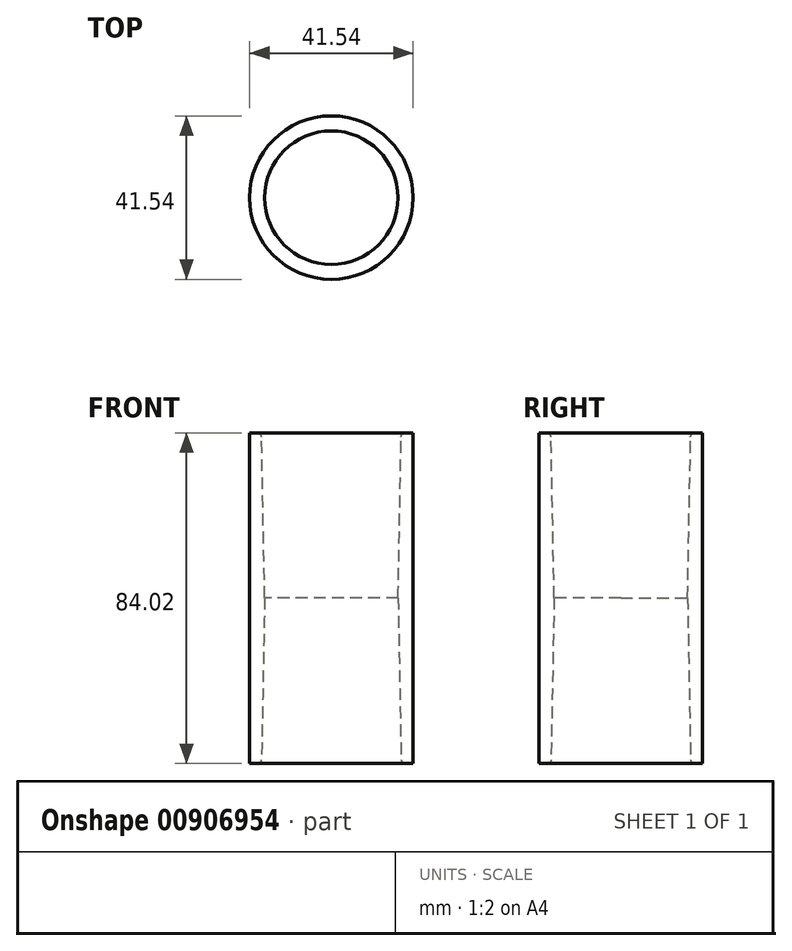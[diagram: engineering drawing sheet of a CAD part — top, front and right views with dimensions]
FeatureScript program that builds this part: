
annotation { "Feature Type Name" : "Feature", "Feature Type Description" : "" }
export const myFeature = defineFeature(function(context is Context, id is Id, definition is map)
    precondition{}
    {
        {
            var Q0;
            Q0=qCreatedBy(makeId("Front.planeOp"),FACE);
            var sketch = newSketch(context, id + "F0", { "sketchPlane" : qUnion([Q0])});
            skLineSegment(sketch, "E0", {"start": v(0, 58.06) * mm, "end": v(0, -71.52) * mm, "construction": true});
            skLineSegment(sketch, "E1", {"start": v(16.95, 0) * mm, "end": v(17.75, 41.92) * mm});
            skLineSegment(sketch, "E2", {"start": v(16.95, 0) * mm, "end": v(17.75, -42.12) * mm});
            skLineSegment(sketch, "E3", {"start": v(17.75, 41.92) * mm, "end": v(20.77, 41.86) * mm});
            skLineSegment(sketch, "E4", {"start": v(20.77, 41.86) * mm, "end": v(20.77, -42.12) * mm});
            skLineSegment(sketch, "E5", {"start": v(20.77, -42.12) * mm, "end": v(17.75, -42.12) * mm});
            skSolve(sketch);
        }
        {
            var Q0;
            Q0=makeQuery(id+"F0.imprint","IMPRINT",FACE,{"disambiguationData":[TD([[makeQuery(id+"F0.imprint","IMPRINT",EDGE,{"derivedFrom":sQuery(id+"F0.wireOp",EDGE,"E1")}),-1.0]])]});
            var Q1;
            Q1=sQuery(id+"F0.wireOp",EDGE,"E0");
            revolve(context, id + "F1", {"surfaceOperationType" : NewSurfaceOperationType.NEW, "entities" : qUnion([Q0]), "axis" : qUnion([Q1]), "revolveType" : RevolveType.FULL});
        }
        {
            var Q0;
            Q0=makeQuery(id+"F1.opRevolve","SWEPT_EDGE",EDGE,{"disambiguationData":[OSD([sQuery(id+"F0.wireOp",EDGE,"E1"),sQuery(id+"F0.wireOp",EDGE,"E3")])]});
            var Q1;
            Q1=makeQuery(id+"F1.opRevolve","SWEPT_EDGE",EDGE,{"disambiguationData":[OSD([sQuery(id+"F0.wireOp",EDGE,"E2"),sQuery(id+"F0.wireOp",EDGE,"E5")])]});
            fillet(context, id + "F2", {"entities" : qUnion([Q0, Q1]), "radius" : 1 * mm, "tangentPropagation" : true, "allowEdgeOverflow" : false});
        }
    });
